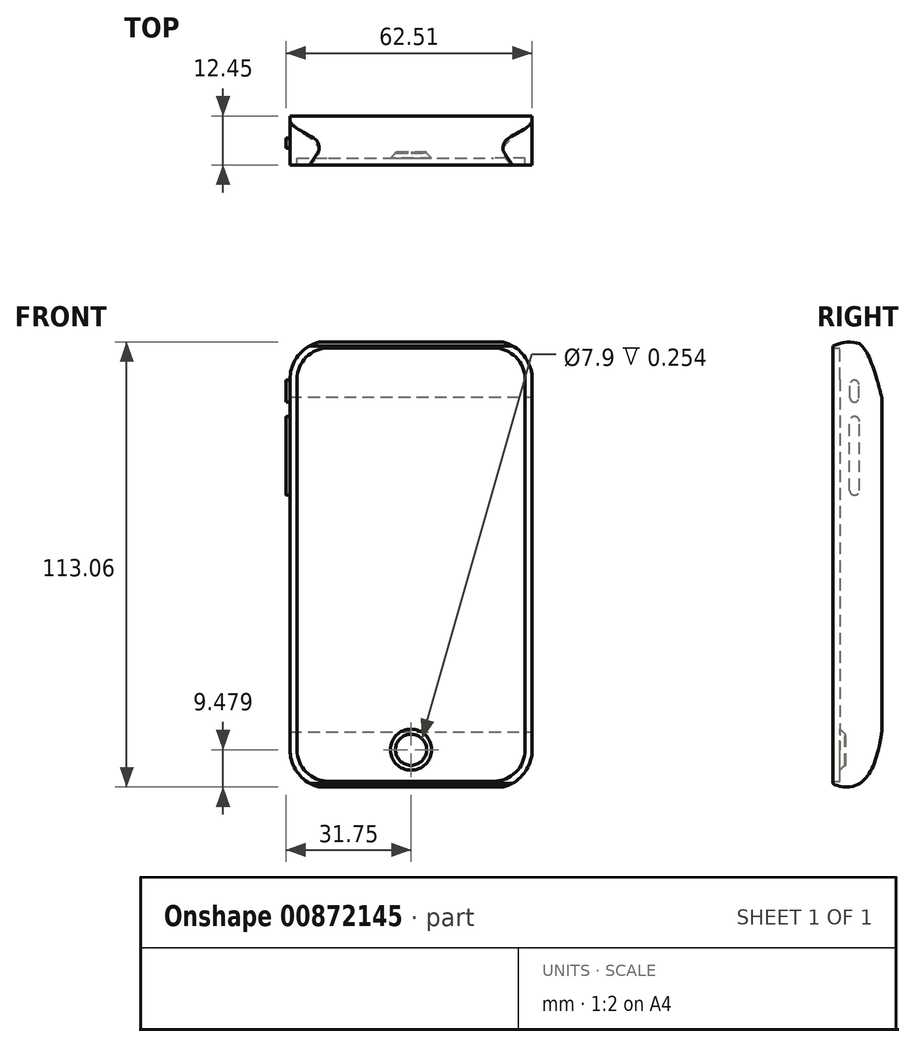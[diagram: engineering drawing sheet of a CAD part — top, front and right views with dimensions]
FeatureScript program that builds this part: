
annotation { "Feature Type Name" : "Feature", "Feature Type Description" : "" }
export const myFeature = defineFeature(function(context is Context, id is Id, definition is map)
    precondition{}
    {
        {
            var Q0;
            Q0=qCreatedBy(makeId("Front.planeOp"),FACE);
            var sketch = newSketch(context, id + "F0", { "sketchPlane" : qUnion([Q0])});
            skLineSegment(sketch, "E0.bottom", {"start": v(20.98, -56.81) * mm, "end": v(-20.98, -56.81) * mm});
            skLineSegment(sketch, "E0.top", {"start": v(20.98, 56.81) * mm, "end": v(-20.98, 56.81) * mm});
            skLineSegment(sketch, "E0.left", {"start": v(30.76, -47.04) * mm, "end": v(30.76, 47.04) * mm});
            skLineSegment(sketch, "E0.right", {"start": v(-30.76, -47.04) * mm, "end": v(-30.76, 47.04) * mm});
            skLineSegment(sketch, "E1", {"start": v(0, 56.81) * mm, "end": v(0, -56.81) * mm, "construction": true});
            skPoint(sketch, "E2", {"position": v(0, 0) * mm});
            skPoint(sketch, "E3.visualSharp", {"position": v(-30.76, 56.81) * mm});
            skArc(sketch, "E3.filletArc", {"start": v(-20.98, 56.81) * mm, "mid": v(-27.9, 53.95) * mm, "end": v(-30.76, 47.04) * mm});
            skPoint(sketch, "E4.visualSharp", {"position": v(30.76, 56.81) * mm});
            skArc(sketch, "E4.filletArc", {"start": v(30.76, 47.04) * mm, "mid": v(27.9, 53.95) * mm, "end": v(20.98, 56.81) * mm});
            skPoint(sketch, "E5.visualSharp", {"position": v(30.76, -56.81) * mm});
            skArc(sketch, "E5.filletArc", {"start": v(20.98, -56.81) * mm, "mid": v(27.9, -53.95) * mm, "end": v(30.76, -47.04) * mm});
            skPoint(sketch, "E6.visualSharp", {"position": v(-30.76, -56.81) * mm});
            skArc(sketch, "E6.filletArc", {"start": v(-30.76, -47.04) * mm, "mid": v(-27.9, -53.95) * mm, "end": v(-20.98, -56.81) * mm});
            skArc(sketch, "E7.0", {"start": v(28.98, 47.04) * mm, "mid": v(26.63, 52.7) * mm, "end": v(20.98, 55.04) * mm});
            skLineSegment(sketch, "E7.1", {"start": v(28.98, -47.04) * mm, "end": v(28.98, 47.04) * mm});
            skLineSegment(sketch, "E7.2", {"start": v(20.98, 55.04) * mm, "end": v(-20.98, 55.04) * mm});
            skArc(sketch, "E7.3", {"start": v(20.98, -55.04) * mm, "mid": v(26.63, -52.7) * mm, "end": v(28.98, -47.04) * mm});
            skArc(sketch, "E7.4", {"start": v(-20.98, 55.04) * mm, "mid": v(-26.63, 52.7) * mm, "end": v(-28.98, 47.04) * mm});
            skLineSegment(sketch, "E7.5", {"start": v(-28.98, -47.04) * mm, "end": v(-28.98, 47.04) * mm});
            skArc(sketch, "E7.6", {"start": v(-28.98, -47.04) * mm, "mid": v(-26.63, -52.7) * mm, "end": v(-20.98, -55.04) * mm});
            skLineSegment(sketch, "E7.7", {"start": v(20.98, -55.04) * mm, "end": v(-20.98, -55.04) * mm});
            skCircle(sketch, "E8", {"center": v(0, -47.04) * mm, "radius": 3.95 * mm});
            skPoint(sketch, "E8.first.point", {"position": v(-3.95, -47.02) * mm});
            skPoint(sketch, "E8.second.point", {"position": v(3.94, -46.75) * mm});
            skPoint(sketch, "E8.third.point", {"position": v(0, -43.1) * mm});
            skSolve(sketch);
        }
        {
            var Q0;
            Q0=makeQuery(id+"F0.imprint","IMPRINT",FACE,{"disambiguationData":[TD([[makeQuery(id+"F0.imprint","IMPRINT",EDGE,{"derivedFrom":sQuery(id+"F0.wireOp",EDGE,"E0.bottom")}),-1.0]])]});
            var Q1;
            Q1=makeQuery(id+"F0.imprint","IMPRINT",FACE,{"disambiguationData":[TD([[makeQuery(id+"F0.imprint","IMPRINT",EDGE,{"derivedFrom":sQuery(id+"F0.wireOp",EDGE,"E7.0")}),1.0]])]});
            var Q2;
            Q2=makeQuery(id+"F0.imprint","IMPRINT",FACE,{"disambiguationData":[TD([[makeQuery(id+"F0.imprint","IMPRINT",EDGE,{"derivedFrom":sQuery(id+"F0.wireOp",EDGE,"E8")}),1.0]])]});
            extrude(context, id + "F1", {"entities" : qUnion([Q0, Q1, Q2]), "depth" : 10.67 * mm, "offsetDistance" : 25.4 * mm});
        }
        {
            var Q0;
            Q0=makeQuery(id+"F0.imprint","IMPRINT",FACE,{"disambiguationData":[TD([[makeQuery(id+"F0.imprint","IMPRINT",EDGE,{"derivedFrom":sQuery(id+"F0.wireOp",EDGE,"E0.bottom")}),-1.0]])]});
            extrude(context, id + "F2", {"entities" : qUnion([Q0]), "operationType" : NewBodyOperationType.ADD, "depth" : 12.45 * mm, "offsetDistance" : 25.4 * mm});
        }
        {
            var Q0;
            Q0=makeQuery(id+"F0.imprint","IMPRINT",FACE,{"disambiguationData":[TD([[makeQuery(id+"F0.imprint","IMPRINT",EDGE,{"derivedFrom":sQuery(id+"F0.wireOp",EDGE,"E8")}),1.0]])]});
            var Q1;
            Q1=sQuery(id+"F0.wireOp",EDGE,"E8");
            extrude(context, id + "F3", {"entities" : qUnion([Q0]), "operationType" : NewBodyOperationType.REMOVE, "surfaceEntities" : qUnion([Q1]), "depth" : 19.05 * mm, "offsetDistance" : 25.4 * mm, "hasSecondDirection" : true, "secondDirectionOppositeDirection" : false, "secondDirectionDepth" : 9.14 * mm});
        }
        {
            var Q0;
            Q0=makeQuery(id+"F3.boolean.opBoolean","INTERSECT",EDGE,{"derivedFrom":[makeQuery(id+"F1.opExtrude","CAP_FACE",FACE,{"disambiguationData":[OSD([sQuery(id+"F0.wireOp",EDGE,"E0.bottom"),sQuery(id+"F0.wireOp",EDGE,"E0.top"),sQuery(id+"F0.wireOp",EDGE,"E0.left"),sQuery(id+"F0.wireOp",EDGE,"E0.right"),sQuery(id+"F0.wireOp",EDGE,"E3.filletArc"),sQuery(id+"F0.wireOp",EDGE,"E4.filletArc"),sQuery(id+"F0.wireOp",EDGE,"E5.filletArc"),sQuery(id+"F0.wireOp",EDGE,"E6.filletArc")])],"isStart":false}),makeQuery(id+"F3.opExtrude","SWEPT_FACE",FACE,{"disambiguationData":[OSD([sQuery(id+"F0.wireOp",EDGE,"E8")])]})]});
            chamfer(context, id + "F4", {"entities" : qUnion([Q0]), "width" : 1.27 * mm, "tangentPropagation" : true});
        }
        {
            var Q0;
            Q0=qCreatedBy(makeId("Right.planeOp"),FACE);
            var sketch = newSketch(context, id + "F5", { "sketchPlane" : qUnion([Q0])});
            skPoint(sketch, "E9", {"position": v(3.58, 0) * mm});
            skFitSpline(sketch, "E10", {"points": [v(0, 42.51) * mm, v(-7.34, 56.48) * mm, v(-12.7, 55.48) * mm], "startDerivative": vector(-16.52, 67.3) * mm, "endDerivative": vector(-29.67, -10.35) * mm});
            skLineSegment(sketch, "E11", {"start": v(0, 0) * mm, "end": v(-7.85, 0) * mm, "construction": true});
            skFitSpline(sketch, "E12.MirrorCS", {"points": [v(0, -42.51) * mm, v(-9.58, -56.49) * mm, v(-12.7, -55.48) * mm], "startDerivative": vector(-7.76, -58.23) * mm, "endDerivative": vector(-10.43, 6.3) * mm});
            skLineSegment(sketch, "E13", {"start": v(0, 42.51) * mm, "end": v(8.7, 42.51) * mm});
            skLineSegment(sketch, "E14", {"start": v(8.7, 42.51) * mm, "end": v(-8.25, 71.91) * mm});
            skLineSegment(sketch, "E15", {"start": v(-8.25, 71.91) * mm, "end": v(-15.38, 57.52) * mm});
            skLineSegment(sketch, "E16", {"start": v(-15.38, 57.52) * mm, "end": v(-12.7, 55.48) * mm});
            skLineSegment(sketch, "E17", {"start": v(0, -42.51) * mm, "end": v(6.57, -51.93) * mm});
            skLineSegment(sketch, "E18", {"start": v(6.57, -51.93) * mm, "end": v(-3.84, -63.5) * mm});
            skLineSegment(sketch, "E19", {"start": v(-3.84, -63.5) * mm, "end": v(-17.8, -53.51) * mm});
            skLineSegment(sketch, "E20", {"start": v(-17.8, -53.51) * mm, "end": v(-12.7, -55.48) * mm});
            skSolve(sketch);
        }
        {
            var Q0;
            Q0=makeQuery(id+"F5.imprint","IMPRINT",FACE,{"disambiguationData":[TD([[makeQuery(id+"F5.imprint","IMPRINT",EDGE,{"derivedFrom":sQuery(id+"F5.wireOp",EDGE,"E10")}),-1.0]])]});
            var Q1;
            Q1=makeQuery(id+"F5.imprint","IMPRINT",FACE,{"disambiguationData":[TD([[makeQuery(id+"F5.imprint","IMPRINT",EDGE,{"derivedFrom":sQuery(id+"F5.wireOp",EDGE,"E12.MirrorCS")}),1.0]])]});
            extrude(context, id + "F6", {"entities" : qUnion([Q0, Q1]), "operationType" : NewBodyOperationType.REMOVE, "endBound" : BoundingType.SYMMETRIC, "oppositeDirection" : true, "depth" : 69.6 * mm, "offsetDistance" : 25.4 * mm});
        }
        {
            var Q0;
            Q0=qCreatedBy(makeId("Right.planeOp"),FACE);
            var sketch = newSketch(context, id + "F7", { "sketchPlane" : qUnion([Q0])});
            skArc(sketch, "E21", {"start": v(-5.64, 36.36) * mm, "mid": v(-6.89, 37.61) * mm, "end": v(-8.14, 36.36) * mm});
            skArc(sketch, "E22", {"start": v(-8.14, 18.86) * mm, "mid": v(-6.89, 17.61) * mm, "end": v(-5.64, 18.86) * mm});
            skLineSegment(sketch, "E23", {"start": v(-5.64, 36.36) * mm, "end": v(-5.64, 18.86) * mm});
            skLineSegment(sketch, "E24", {"start": v(-8.14, 36.36) * mm, "end": v(-8.14, 18.86) * mm});
            skArc(sketch, "E25", {"start": v(-5.8, 45.73) * mm, "mid": v(-6.91, 46.84) * mm, "end": v(-8.03, 45.73) * mm});
            skArc(sketch, "E26", {"start": v(-8.03, 42.37) * mm, "mid": v(-6.91, 41.25) * mm, "end": v(-5.8, 42.37) * mm});
            skLineSegment(sketch, "E27", {"start": v(-5.8, 45.73) * mm, "end": v(-5.8, 42.37) * mm});
            skLineSegment(sketch, "E28", {"start": v(-8.03, 45.73) * mm, "end": v(-8.03, 42.37) * mm});
            skSolve(sketch);
        }
        {
            var Q0;
            Q0 = qSketchRegion(id + "F7", true);
            extrude(context, id + "F8", {"entities" : qUnion([Q0]), "operationType" : NewBodyOperationType.ADD, "oppositeDirection" : true, "depth" : 31.75 * mm, "offsetDistance" : 25.4 * mm});
        }
    });
